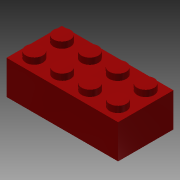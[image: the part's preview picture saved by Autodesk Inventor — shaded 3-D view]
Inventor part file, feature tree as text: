
AUTODESK INVENTOR PART (.ipt)
format: ipt  version: 2015 (Build 190159000, 159)  size: 263,680 bytes
history: native  units: in
note: dims shown in document units (in); Inventor stores cm internally (conversion verified against a paired STEP export)
features: extrude x7, sketch x7, plane x5, fillet x1
ambient origin geometry x8: Origin, YZ Plane, XZ Plane, XY Plane, X Axis, Y Axis, Z Axis, Center Point
bodies: Solid1 (feature_tree)
feature tree (20):
  extrude  "Extrusion1"  Depth=0.62in
  plane  "Work Plane1"
  extrude  "Extrusion2"  TaperAngle=0.0deg  [1 undecoded]
  plane  "Work Plane2"
  extrude  "Extrusion3"  Depth=0.19in
  plane  "Work Plane3"
  extrude  "Extrusion4"  Depth=0.19in
  extrude  "Extrusion5"  Depth=0.19in
  fillet  "Fillet2"  Radius=0.19in
  plane  "Work Plane4"
  extrude  "Extrusion6"  Depth=0.07in TaperAngle=0.0deg
  plane  "Work Plane5"
  extrude  "Extrusion7"  Depth=0.02in
  sketch  "Sketch1"  dims[d0=1.25in d2=0.62in]
  sketch  "Sketch2"  dims[d3=0.38in d4=0.0in d5=0.0in]
  sketch  "Sketch3"  dims[d17=0.19in d19=0.19in]
  sketch  "Sketch4"  dims[d21=0.19in d23=0.19in]
  sketch  "Sketch5"  dims[d25=0.19in d29=0.19in d30=0.19in]
  sketch  "Sketch6"  dims[d31=0.19in d32=0.07in d33=0.0in]
  sketch  "Sketch7"  dims[d34=0.0in d48=0.025in d49=0.01in d50=0.025in d51=0.01in d52=0.025in d53=0.01in d54=0.025in d55=0.01in d58=0.155in d65=0.025in d66=0.01in d67=0.025in d68=0.01in d69=0.33in d70=0.0in d71=0.0in d78=0.26in d79=0.26in d80=0.26in d81=0.225in d82=0.225in d83=0.225in d84=0.33in d85=0.0in d91=0.26in d92=0.035in d93=0.035in d94=0.2697in d95=0.0in d97=0.005in d98=0.0in d104=0.035in d106=1.0in d107=0.0in d108=0.02in d110=0.0in d111=0.035in d112=0.02in d113=1.0in d114=0.0in]
note: 1 required parameter value undecoded (feature->parameter linkage not recoverable at this tier; creation-order binding heuristic only, values carry confidence <= 0.55)
